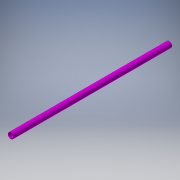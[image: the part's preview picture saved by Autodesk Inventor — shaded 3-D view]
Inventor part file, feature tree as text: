
AUTODESK INVENTOR PART (.ipt)
format: ipt  version: 2018.2 (Build 222227000, 227)  size: 107,008 bytes
history: native  units: in
note: dims shown in document units (in); Inventor stores cm internally (conversion verified against a paired STEP export)
features: extrude x1, sketch x1
ambient origin geometry x8: Origin, YZ Plane, XZ Plane, XY Plane, X Axis, Y Axis, Z Axis, Center Point
bodies: Solid1 (feature_tree)
feature tree (2):
  extrude  "Extrusion1"  Depth=35.554in
  sketch  "Sketch1"  dims[d0=1.315in d1=1.0in d2=35.554in d3=0.0in]
